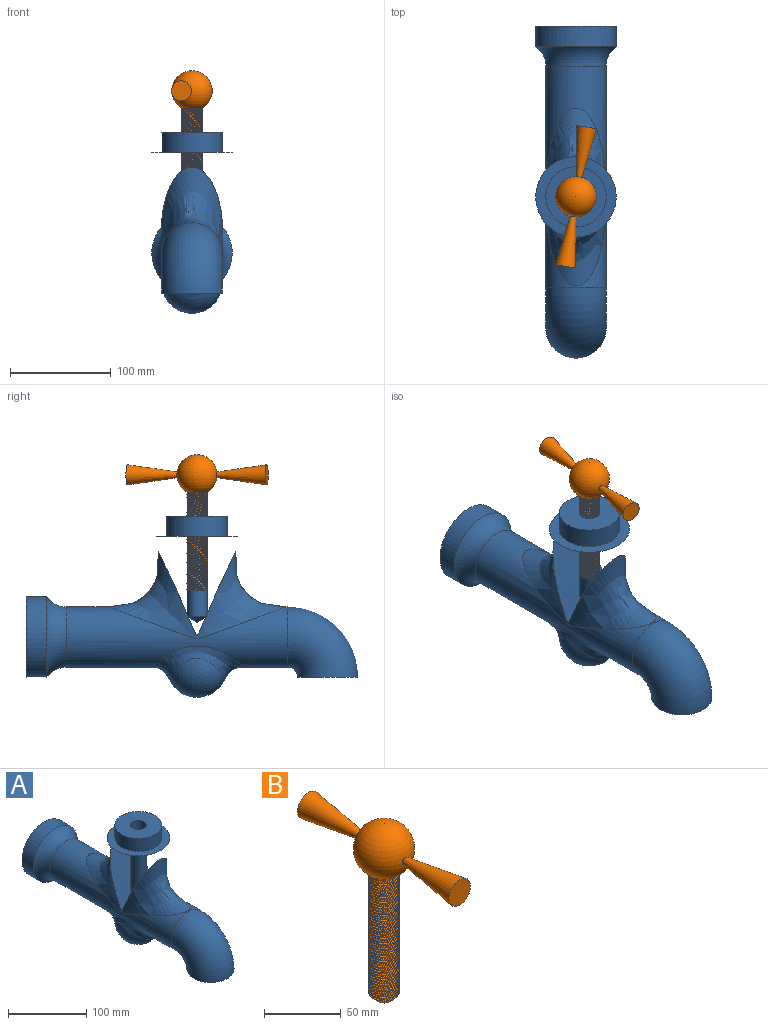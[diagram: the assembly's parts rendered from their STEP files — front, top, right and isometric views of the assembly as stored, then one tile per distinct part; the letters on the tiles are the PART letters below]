
ASSEMBLY  parts=2 mates=1
PART A: 15 faces, bbox 119.1x335.8x180 mm
  f0: cylinder r=30mm len=220mm, axis (0,-1,0), area 26107.6mm2, adj f2,f5,f8,f12
  f1: plane 60x60mm, normal (0,0,-1), area 2827.4mm2, adj f2
  f2: torus R=40mm, axis (1,0,0), area 11843.5mm2, adj f0,f1
  f3: plane 80x80mm, normal (0,0,1), area 2199.1mm2, adj f4,f9
  f4: cone r=40mm half-angle=5.7deg, axis (0,0,1), area 11242.1mm2, adj f3,f5
  f5: bspline ~176.25x85.77mm, area 14106.9mm2, adj f0,f4
  f6: cylinder r=40mm len=80mm, axis (0,1,0), area 5026.5mm2, adj f7,f8
  f7: plane 80x80mm, normal (0,1,0), area 5026.5mm2, adj f6
  f8: torus R=55mm, axis (0,1,0), area 4869.7mm2, adj f0,f6
  f9: cylinder r=30mm len=60mm, axis (0,0,-1), area 3769.9mm2, adj f3,f10
  f10: plane 60x60mm, normal (0,0,1), area 2513.3mm2, adj f9,f14
  f11: sphere r=30mm, area 5222.9mm2, adj f12
  f12: bspline ~91.61x57.2mm, area 3957.8mm2, adj f0,f11
  f13: cone r=0mm half-angle=59deg, axis (0,0,1), area 366.5mm2, adj f14
  f14: cylinder r=10mm len=100mm, axis (0,0,1), area 6283.2mm2, adj f10,f13
PART B: 13 faces, bbox 40x140x140 mm
  f0: sphere r=20mm, area 4639.3mm2, adj f1,f3,f5,f9
  f1: cylinder r=10mm len=97.68mm, axis (0,0,-1), area 2811.4mm2, adj f0,f7,f8,f11,f12
  f2: plane 10x10mm, normal (0,0,-1), area 78.5mm2, adj f7
  f3: cone r=10mm half-angle=8.1deg, axis (0,-1,0), area 2043.7mm2, adj f0,f4
  f4: plane 20x20mm, normal (0,-1,0), area 314.2mm2, adj f3
  f5: cone r=10mm half-angle=8.1deg, axis (0,1,0), area 2043.7mm2, adj f0,f6
  f6: plane 20x20mm, normal (0,1,0), area 314.2mm2, adj f5
  f7: cone r=5mm half-angle=45deg, axis (0,0,1), area 308.4mm2, adj f1,f2,f8,f11
  f8: cone r=5mm half-angle=45deg, axis (0,0,1), area 6.6mm2, adj f1,f7,f12
  f9: cylinder r=10mm len=19.96mm, axis (0,0,1), area 15.3mm2, adj f0,f10,f12
  f10: plane 1x0.87mm, normal (0,-1,0), area 0.4mm2, adj f9,f11,f12
  f11: bspline ~99.76x23.09mm, area 2877mm2, adj f1,f7,f10,f12
  f12: bspline ~99.76x23.09mm, area 2908mm2, adj f1,f8,f9,f10,f11
PLACE A t=(-40.08,107.21,-49.01)mm fixed
PLACE B rot(axis=(0,0,1),171.3deg) t=(-40.08,-62.79,-7.73)mm
MATE cylindrical B.f1 <-> A.f9  axis (0,0,-1) through (-40.08,-62.79,46.11)mm
